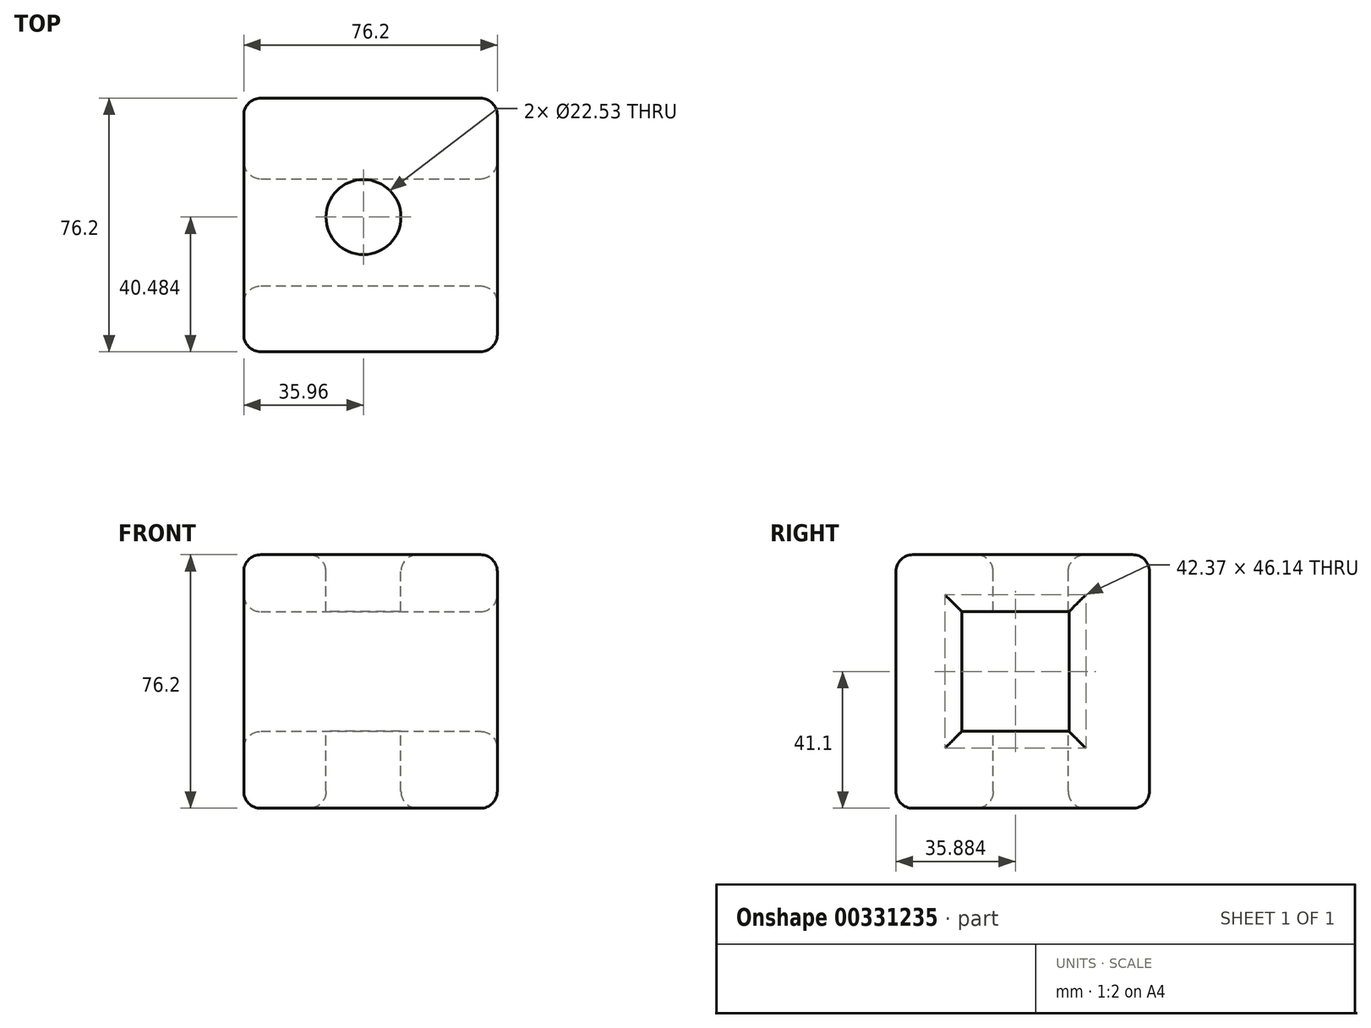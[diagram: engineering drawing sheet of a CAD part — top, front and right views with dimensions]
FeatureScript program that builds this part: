
annotation { "Feature Type Name" : "Feature", "Feature Type Description" : "" }
export const myFeature = defineFeature(function(context is Context, id is Id, definition is map)
    precondition{}
    {
        {
            var Q0;
            Q0=qCreatedBy(makeId("Top.planeOp"),FACE);
            var sketch = newSketch(context, id + "F0", { "sketchPlane" : qUnion([Q0])});
            skLineSegment(sketch, "E0.bottom", {"start": v(0, 0) * mm, "end": v(76.2, 0) * mm});
            skLineSegment(sketch, "E0.top", {"start": v(0, 76.2) * mm, "end": v(76.2, 76.2) * mm});
            skLineSegment(sketch, "E0.left", {"start": v(0, 0) * mm, "end": v(0, 76.2) * mm});
            skLineSegment(sketch, "E0.right", {"start": v(76.2, 0) * mm, "end": v(76.2, 76.2) * mm});
            skSolve(sketch);
        }
        {
            var Q0;
            Q0 = qSketchRegion(id + "F0", true);
            extrude(context, id + "F1", {"entities" : qUnion([Q0]), "depth" : 76.2 * mm});
        }
        {
            var Q0;
            Q0=makeQuery(id+"F1.opExtrude","CAP_FACE",FACE,{"disambiguationData":[OSD([sQuery(id+"F0.wireOp",EDGE,"E0.bottom"),sQuery(id+"F0.wireOp",EDGE,"E0.top"),sQuery(id+"F0.wireOp",EDGE,"E0.left"),sQuery(id+"F0.wireOp",EDGE,"E0.right")])],"isStart":false});
            var sketch = newSketch(context, id + "F2", { "sketchPlane" : qUnion([Q0])});
            skCircle(sketch, "E1", {"center": v(35.96, 40.48) * mm, "radius": 11.27 * mm});
            skSolve(sketch);
        }
        {
            var Q0;
            Q0=makeQuery(id+"F2.imprint","IMPRINT",FACE,{"disambiguationData":[TD([[makeQuery(id+"F2.imprint","IMPRINT",EDGE,{"derivedFrom":sQuery(id+"F2.wireOp",EDGE,"E1")}),1.0]])]});
            extrude(context, id + "F3", {"entities" : qUnion([Q0]), "operationType" : NewBodyOperationType.REMOVE, "endBound" : BoundingType.THROUGH_ALL, "oppositeDirection" : true, "depth" : 25.4 * mm});
        }
        {
            var Q0;
            Q0=makeQuery(id+"F1.opExtrude","SWEPT_FACE",FACE,{"disambiguationData":[OSD([sQuery(id+"F0.wireOp",EDGE,"E0.right")])]});
            var sketch = newSketch(context, id + "F4", { "sketchPlane" : qUnion([Q0])});
            skLineSegment(sketch, "E2.bottom", {"start": v(51.99, 59.1) * mm, "end": v(19.78, 59.1) * mm});
            skLineSegment(sketch, "E2.top", {"start": v(51.99, 23.1) * mm, "end": v(19.78, 23.1) * mm});
            skLineSegment(sketch, "E2.left", {"start": v(51.99, 59.1) * mm, "end": v(51.99, 23.1) * mm});
            skLineSegment(sketch, "E2.right", {"start": v(19.78, 59.1) * mm, "end": v(19.78, 23.1) * mm});
            skSolve(sketch);
        }
        {
            var Q0;
            Q0=makeQuery(id+"F4.imprint","IMPRINT",FACE,{"disambiguationData":[TD([[makeQuery(id+"F4.imprint","IMPRINT",EDGE,{"derivedFrom":sQuery(id+"F4.wireOp",EDGE,"E2.bottom")}),1.0]])]});
            extrude(context, id + "F5", {"entities" : qUnion([Q0]), "operationType" : NewBodyOperationType.REMOVE, "endBound" : BoundingType.THROUGH_ALL, "oppositeDirection" : true, "depth" : 25.4 * mm});
        }
        {
            var Q0;
            Q0=makeQuery(id+"F1.opExtrude","CAP_EDGE",EDGE,{"disambiguationData":[OSD([sQuery(id+"F0.wireOp",EDGE,"E0.bottom")])],"isStart":false});
            var Q1;
            Q1=makeQuery(id+"F1.opExtrude","CAP_EDGE",EDGE,{"disambiguationData":[OSD([sQuery(id+"F0.wireOp",EDGE,"E0.right")])],"isStart":false});
            var Q2;
            Q2=makeQuery(id+"F1.opExtrude","CAP_EDGE",EDGE,{"disambiguationData":[OSD([sQuery(id+"F0.wireOp",EDGE,"E0.top")])],"isStart":false});
            var Q3;
            Q3=makeQuery(id+"F1.opExtrude","CAP_EDGE",EDGE,{"disambiguationData":[OSD([sQuery(id+"F0.wireOp",EDGE,"E0.left")])],"isStart":false});
            var Q4;
            Q4=makeQuery(id+"F1.opExtrude","SWEPT_FACE",FACE,{"disambiguationData":[OSD([sQuery(id+"F0.wireOp",EDGE,"E0.bottom")])]});
            var Q5;
            Q5=makeQuery(id+"F1.opExtrude","CAP_EDGE",EDGE,{"disambiguationData":[OSD([sQuery(id+"F0.wireOp",EDGE,"E0.right")])],"isStart":true});
            var Q6;
            Q6=makeQuery(id+"F5.boolean.opBoolean","COPY",EDGE,{"derivedFrom":makeQuery(id+"F5.opExtrude","CAP_EDGE",EDGE,{"disambiguationData":[OSD([sQuery(id+"F4.wireOp",EDGE,"E2.top")])],"isStart":true})});
            var Q7;
            Q7=makeQuery(id+"F5.boolean.opBoolean","COPY",EDGE,{"derivedFrom":makeQuery(id+"F5.opExtrude","CAP_EDGE",EDGE,{"disambiguationData":[OSD([sQuery(id+"F4.wireOp",EDGE,"E2.left")])],"isStart":true})});
            var Q8;
            Q8=makeQuery(id+"F1.opExtrude","SWEPT_FACE",FACE,{"disambiguationData":[OSD([sQuery(id+"F0.wireOp",EDGE,"E0.right")])]});
            var Q9;
            Q9=makeQuery(id+"F1.opExtrude","SWEPT_FACE",FACE,{"disambiguationData":[OSD([sQuery(id+"F0.wireOp",EDGE,"E0.top")])]});
            var Q10;
            Q10=makeQuery(id+"F1.opExtrude","CAP_FACE",FACE,{"disambiguationData":[OSD([sQuery(id+"F0.wireOp",EDGE,"E0.bottom"),sQuery(id+"F0.wireOp",EDGE,"E0.top"),sQuery(id+"F0.wireOp",EDGE,"E0.left"),sQuery(id+"F0.wireOp",EDGE,"E0.right")])],"isStart":true});
            fillet(context, id + "F6", {"entities" : qUnion([Q0, Q1, Q2, Q3, Q4, Q5, Q6, Q7, Q8, Q9, Q10]), "radius" : 5.08 * mm, "tangentPropagation" : true, "allowEdgeOverflow" : false});
        }
        {
            var Q0;
            Q0=makeQuery(id+"F1.opExtrude","CAP_FACE",FACE,{"disambiguationData":[OSD([sQuery(id+"F0.wireOp",EDGE,"E0.bottom"),sQuery(id+"F0.wireOp",EDGE,"E0.top"),sQuery(id+"F0.wireOp",EDGE,"E0.left"),sQuery(id+"F0.wireOp",EDGE,"E0.right")])],"isStart":false});
            var Q1;
            Q1=makeQuery(id+"F1.opExtrude","SWEPT_FACE",FACE,{"disambiguationData":[OSD([sQuery(id+"F0.wireOp",EDGE,"E0.left")])]});
            fillet(context, id + "F7", {"entities" : qUnion([Q0, Q1]), "radius" : 5.08 * mm, "tangentPropagation" : true, "allowEdgeOverflow" : false});
        }
    });
